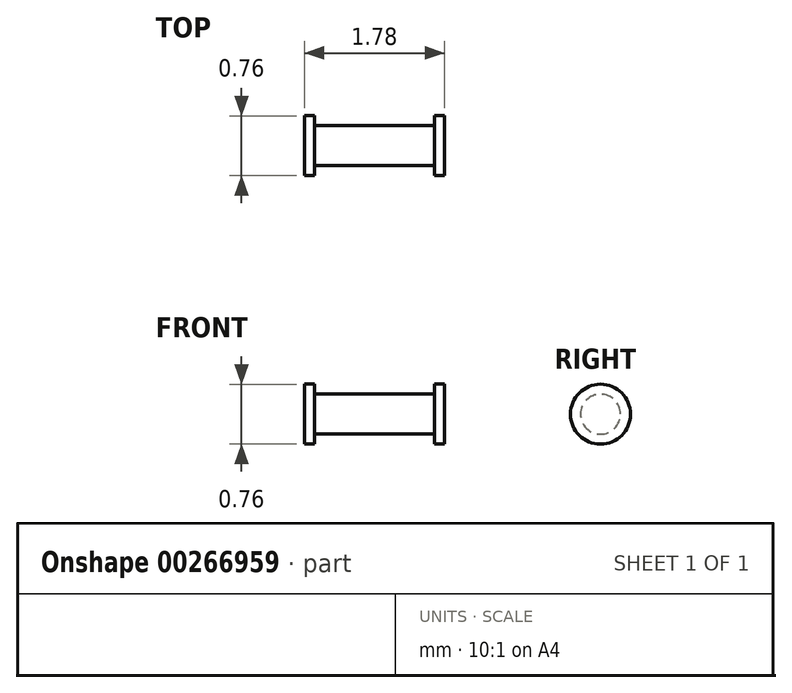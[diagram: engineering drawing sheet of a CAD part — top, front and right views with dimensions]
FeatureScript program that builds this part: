
annotation { "Feature Type Name" : "Feature", "Feature Type Description" : "" }
export const myFeature = defineFeature(function(context is Context, id is Id, definition is map)
    precondition{}
    {
        {
            var Q0;
            Q0=qCreatedBy(makeId("Front.planeOp"),FACE);
            var sketch = newSketch(context, id + "F0", { "sketchPlane" : qUnion([Q0])});
            skLineSegment(sketch, "E0", {"start": v(0, 0) * mm, "end": v(0, 0.38) * mm});
            skLineSegment(sketch, "E1", {"start": v(1.78, 0) * mm, "end": v(0, 0) * mm});
            skLineSegment(sketch, "E2", {"start": v(0, 0.38) * mm, "end": v(0.13, 0.38) * mm});
            skLineSegment(sketch, "E3", {"start": v(1.78, 0) * mm, "end": v(1.78, 0.38) * mm});
            skLineSegment(sketch, "E4", {"start": v(1.78, 0.38) * mm, "end": v(1.65, 0.38) * mm});
            skLineSegment(sketch, "E5", {"start": v(1.65, 0.38) * mm, "end": v(1.65, 0.25) * mm});
            skLineSegment(sketch, "E6", {"start": v(1.65, 0.25) * mm, "end": v(0.13, 0.25) * mm});
            skLineSegment(sketch, "E7", {"start": v(0.13, 0.25) * mm, "end": v(0.13, 0.38) * mm});
            skSolve(sketch);
        }
        {
            var Q0;
            Q0 = qSketchRegion(id + "F0", true);
            var Q1;
            Q1=sQuery(id+"F0.wireOp",EDGE,"E1");
            revolve(context, id + "F1", {"entities" : qUnion([Q0]), "axis" : qUnion([Q1]), "revolveType" : RevolveType.FULL});
        }
    });
